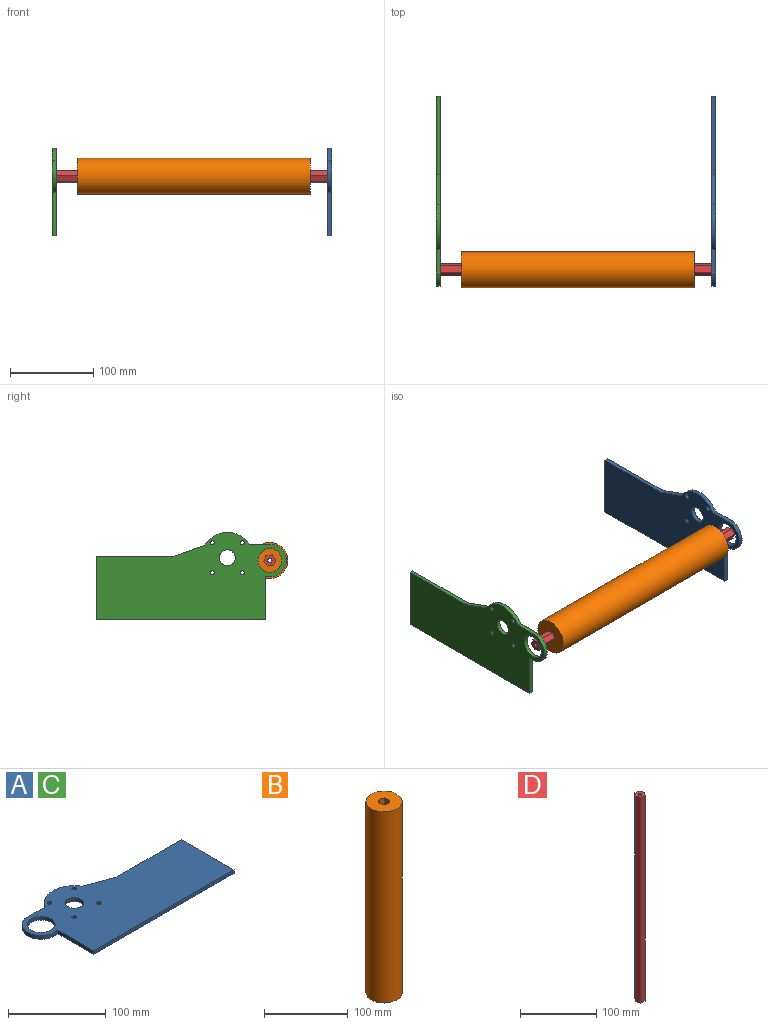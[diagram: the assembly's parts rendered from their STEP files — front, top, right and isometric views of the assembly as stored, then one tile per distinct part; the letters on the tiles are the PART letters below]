
ASSEMBLY  parts=4 mates=3
PART A: 17 faces, bbox 228x104.9x4.6 mm
  f0: plane 36.3x13.17mm, normal (0.34,0.94,0), area 178.5mm2, adj f1,f14,f15,f16
  f1: cylinder r=30.62mm len=52.92mm, axis (0,0,-1), area 295.4mm2, adj f0,f2,f15,f16
  f2: plane 29.93x4.62mm, normal (0,1,0), area 138.3mm2, adj f1,f3,f15,f16
  f3: cylinder r=19.71mm len=38.1mm, axis (0,0,-1), area 239.1mm2, adj f2,f4,f15,f16
  f4: plane 10.12x4.62mm, normal (0,-1,0), area 46.8mm2, adj f3,f5,f15,f16
  f5: plane 52.07x4.62mm, normal (-1,0,0), area 240.7mm2, adj f4,f6,f15,f16
  f6: plane 203.2x4.62mm, normal (0,-1,0), area 939.4mm2, adj f5,f7,f15,f16
  f7: plane 76.09x4.62mm, normal (1,0,0), area 351.7mm2, adj f6,f14,f15,f16
  f8: cylinder r=14.25mm len=28.5mm, axis (0,0,-1), area 413.9mm2, adj f15,f16
  f9: cylinder r=9.53mm len=19.05mm, axis (0,0,-1), area 276.7mm2, adj f15,f16
  f10: cylinder r=2.41mm len=4.83mm, axis (0,0,-1), area 70.1mm2, adj f15,f16
  f11: cylinder r=2.41mm len=4.83mm, axis (0,0,-1), area 70.1mm2, adj f15,f16
  f12: cylinder r=2.41mm len=4.83mm, axis (0,0,-1), area 70.1mm2, adj f15,f16
  f13: cylinder r=2.41mm len=4.83mm, axis (0,0,-1), area 70.1mm2, adj f15,f16
  f14: plane 94.17x4.62mm, normal (0,1,0), area 435.3mm2, adj f0,f7,f15,f16
  f15: plane 227.99x104.93mm, normal (0,0,1), area 17073.8mm2, adj f0,f1,f2,f3,f4,f5,f6,f7
  f16: plane 227.99x104.93mm, normal (0,0,-1), area 17073.8mm2, adj f0,f1,f2,f3,f4,f5,f6,f7
PART B: 9 faces, bbox 43.2x43.2x279.4 mm
  f0: plane 279.4x6.72mm, normal (-0.4,-0.92,0), area 2048.7mm2, adj f1,f5,f7,f8
  f1: plane 279.4x7.29mm, normal (-0.99,-0.11,0), area 2048.7mm2, adj f0,f2,f7,f8
  f2: plane 279.4x5.9mm, normal (-0.59,0.81,0), area 2048.7mm2, adj f1,f3,f7,f8
  f3: plane 279.4x6.72mm, normal (0.4,0.92,0), area 2048.7mm2, adj f2,f4,f7,f8
  f4: plane 279.4x7.29mm, normal (0.99,0.11,0), area 2048.7mm2, adj f3,f5,f7,f8
  f5: plane 279.4x5.9mm, normal (0.59,-0.81,0), area 2048.7mm2, adj f0,f4,f7,f8
  f6: cylinder r=21.59mm len=279.4mm, axis (0,0,-1), area 37901.7mm2, adj f7,f8
  f7: plane 43.18x43.18mm, normal (0,0,1), area 1324.7mm2, adj f0,f1,f2,f3,f4,f5,f6
  f8: plane 43.18x43.18mm, normal (0,0,-1), area 1324.7mm2, adj f0,f1,f2,f3,f4,f5,f6
PART C: same geometry as A
PART D: 9 faces, bbox 14.4x13.8x330.2 mm
  f0: plane 330.2x6.91mm, normal (0.94,0.33,0), area 2421.1mm2, adj f1,f6,f7,f8
  f1: plane 330.2x7.21mm, normal (0.18,0.98,0), area 2421.1mm2, adj f0,f2,f7,f8
  f2: plane 330.2x5.58mm, normal (-0.76,0.65,0), area 2421.1mm2, adj f1,f3,f7,f8
  f3: plane 330.2x6.91mm, normal (-0.94,-0.33,0), area 2421.1mm2, adj f2,f4,f7,f8
  f4: plane 330.2x7.21mm, normal (-0.18,-0.98,0), area 2421.1mm2, adj f3,f6,f7,f8
  f5: cylinder r=2.55mm len=330.2mm, axis (0,0,-1), area 5296.1mm2, adj f7,f8
  f6: plane 330.2x5.58mm, normal (0.76,-0.65,0), area 2421.1mm2, adj f0,f4,f7,f8
  f7: plane 14.42x13.82mm, normal (0,0,1), area 119.2mm2, adj f0,f1,f2,f3,f4,f5,f6
  f8: plane 14.42x13.82mm, normal (0,0,-1), area 119.2mm2, adj f0,f1,f2,f3,f4,f5,f6
PLACE A rot(axis=(0.58,0.58,0.58),120deg) t=(-143.73,-59.94,162.72)mm
PLACE B rot(axis=(-0.03,-1,0.03),90deg) t=(-164.5,-236.53,154.38)mm
PLACE C rot(axis=(0.58,0.58,0.58),120deg) t=(-473.93,-59.94,162.72)mm
PLACE D rot(axis=(-0.71,-0.06,0.71),172.9deg) t=(-139.1,-157.38,332.9)mm
MATE revolute D.f5 <-> A.f3  axis (1,0,0) through (-139.1,-187.27,218.07)mm
MATE revolute D.f5 <-> C.f3  axis (-1,0,0) through (-469.3,-187.27,218.07)mm
MATE fastened B.f3 <-> D.f1  axis (0,0.94,0.35) through (-304.2,-193.22,215.85)mm
